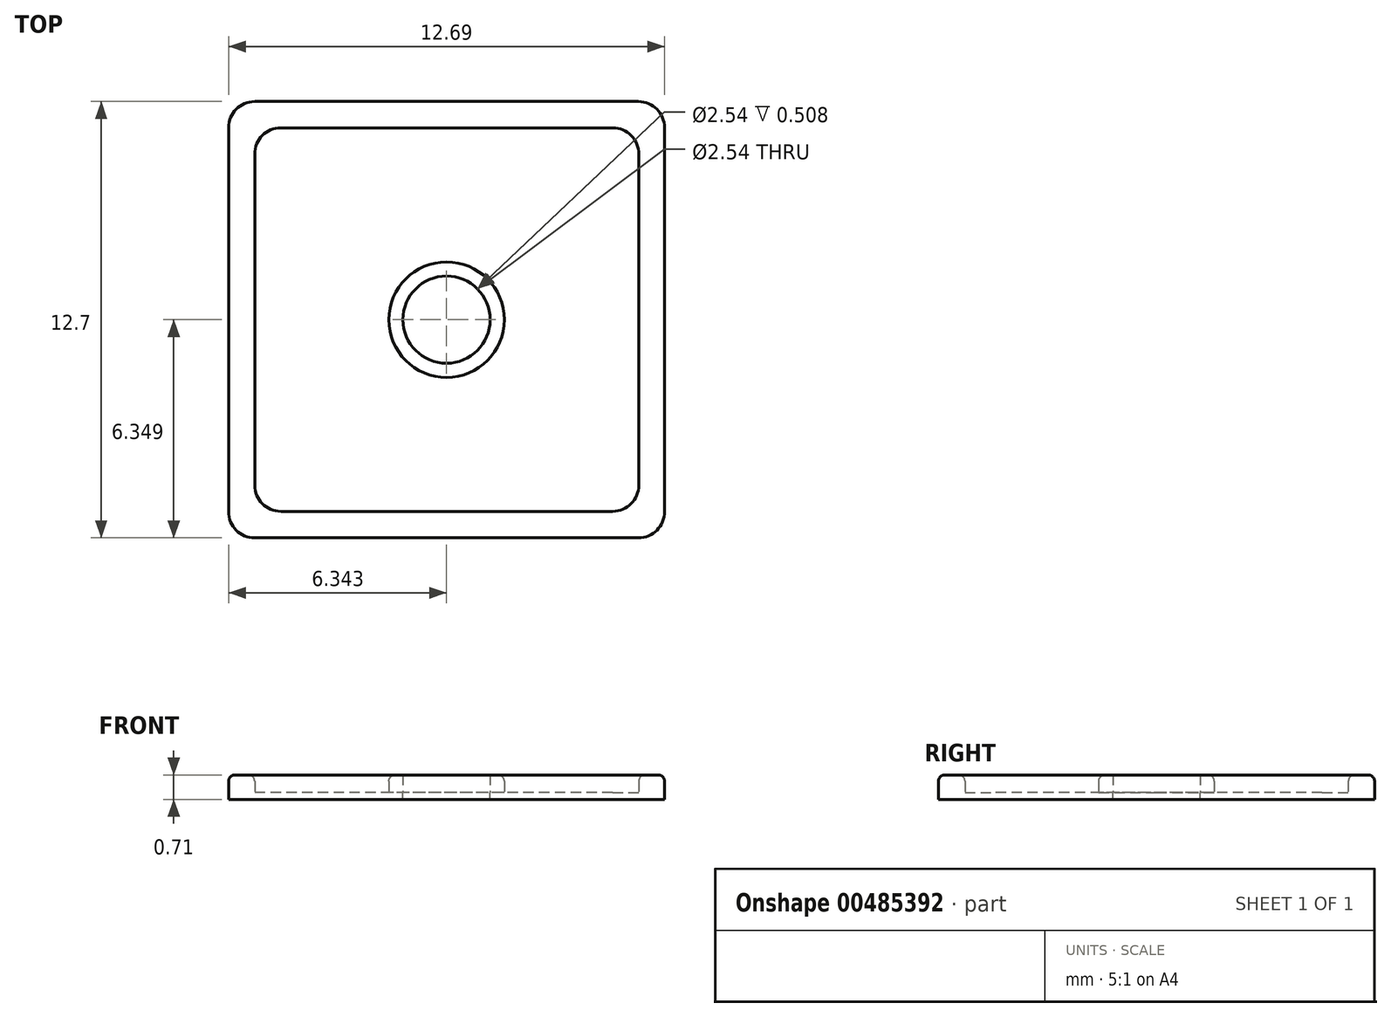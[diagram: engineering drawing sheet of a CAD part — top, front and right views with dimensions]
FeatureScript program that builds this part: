
annotation { "Feature Type Name" : "Feature", "Feature Type Description" : "" }
export const myFeature = defineFeature(function(context is Context, id is Id, definition is map)
    precondition{}
    {
        {
            var Q0;
            Q0=qCreatedBy(makeId("Top.planeOp"),FACE);
            var sketch = newSketch(context, id + "F0", { "sketchPlane" : qUnion([Q0])});
            skLineSegment(sketch, "E0.bottom", {"start": v(0, 0) * mm, "end": v(-12.7, 0) * mm});
            skLineSegment(sketch, "E0.top", {"start": v(0, 12.7) * mm, "end": v(-12.7, 12.7) * mm});
            skLineSegment(sketch, "E0.left", {"start": v(0, 0) * mm, "end": v(0, 12.7) * mm});
            skLineSegment(sketch, "E0.right", {"start": v(-12.7, 0) * mm, "end": v(-12.7, 12.7) * mm});
            skLineSegment(sketch, "E1", {"start": v(-6.35, 12.7) * mm, "end": v(-6.35, 11.93) * mm});
            skPoint(sketch, "E1.endSnap0", {"position": v(-6.35, 12.7) * mm});
            skLineSegment(sketch, "E2", {"start": v(-12.7, 6.35) * mm, "end": v(-11.93, 6.35) * mm});
            skLineSegment(sketch, "E3", {"start": v(-6.35, 11.93) * mm, "end": v(-11.93, 11.93) * mm});
            skLineSegment(sketch, "E4", {"start": v(-11.93, 11.93) * mm, "end": v(-11.93, 6.35) * mm});
            skLineSegment(sketch, "E5", {"start": v(-6.35, 0) * mm, "end": v(-6.35, 0.77) * mm});
            skLineSegment(sketch, "E6", {"start": v(0, 6.35) * mm, "end": v(-0.75, 6.35) * mm});
            skLineSegment(sketch, "E7", {"start": v(-0.75, 6.35) * mm, "end": v(-0.75, 0.77) * mm});
            skLineSegment(sketch, "E8", {"start": v(-0.75, 0.77) * mm, "end": v(-6.35, 0.77) * mm});
            skLineSegment(sketch, "E9", {"start": v(-6.35, 0.77) * mm, "end": v(-11.93, 0.77) * mm});
            skLineSegment(sketch, "E10", {"start": v(-11.93, 0.77) * mm, "end": v(-11.93, 6.35) * mm});
            skLineSegment(sketch, "E11", {"start": v(-6.35, 11.93) * mm, "end": v(-0.75, 11.93) * mm});
            skLineSegment(sketch, "E12", {"start": v(-0.75, 11.93) * mm, "end": v(-0.75, 6.35) * mm});
            skPoint(sketch, "E13", {"position": v(-6.35, 6.35) * mm});
            skSolve(sketch);
        }
        {
            var Q0;
            {var subQ4=sQuery(id+"F0.wireOp",EDGE,"E1");Q0=makeQuery(id+"F0.imprint","IMPRINT",FACE,{"disambiguationData":[TD([[makeQuery(id+"F0.imprint","IMPRINT",EDGE,{"derivedFrom":subQ4}),-1.0]])]});}
            var Q1;
            {var subQ4=sQuery(id+"F0.wireOp",EDGE,"E1");Q1=makeQuery(id+"F0.imprint","IMPRINT",FACE,{"disambiguationData":[TD([[makeQuery(id+"F0.imprint","IMPRINT",EDGE,{"derivedFrom":subQ4}),1.0]])]});}
            var Q2;
            {var subQ1=sQuery(id+"F0.wireOp",EDGE,"E5");Q2=makeQuery(id+"F0.imprint","IMPRINT",FACE,{"disambiguationData":[TD([[makeQuery(id+"F0.imprint","IMPRINT",EDGE,{"derivedFrom":subQ1}),-1.0]])]});}
            var Q3;
            {var subQ4=sQuery(id+"F0.wireOp",EDGE,"E2");Q3=makeQuery(id+"F0.imprint","IMPRINT",FACE,{"disambiguationData":[TD([[makeQuery(id+"F0.imprint","IMPRINT",EDGE,{"derivedFrom":subQ4}),-1.0]])]});}
            extrude(context, id + "F1", {"entities" : qUnion([Q0, Q1, Q2, Q3]), "depth" : 0.5 * mm});
        }
        {
            var Q0;
            Q0=makeQuery(id+"F0.imprint","IMPRINT",FACE,{"disambiguationData":[TD([[makeQuery(id+"F0.imprint","IMPRINT",EDGE,{"derivedFrom":sQuery(id+"F0.wireOp",EDGE,"E3")}),1.0]])]});
            var Q1;
            {var subQ4=sQuery(id+"F0.wireOp",EDGE,"E1");Q1=makeQuery(id+"F0.imprint","IMPRINT",FACE,{"disambiguationData":[TD([[makeQuery(id+"F0.imprint","IMPRINT",EDGE,{"derivedFrom":subQ4}),-1.0]])]});}
            var Q2;
            {var subQ4=sQuery(id+"F0.wireOp",EDGE,"E2");Q2=makeQuery(id+"F0.imprint","IMPRINT",FACE,{"disambiguationData":[TD([[makeQuery(id+"F0.imprint","IMPRINT",EDGE,{"derivedFrom":subQ4}),-1.0]])]});}
            var Q3;
            {var subQ1=sQuery(id+"F0.wireOp",EDGE,"E5");Q3=makeQuery(id+"F0.imprint","IMPRINT",FACE,{"disambiguationData":[TD([[makeQuery(id+"F0.imprint","IMPRINT",EDGE,{"derivedFrom":subQ1}),-1.0]])]});}
            var Q4;
            {var subQ4=sQuery(id+"F0.wireOp",EDGE,"E1");Q4=makeQuery(id+"F0.imprint","IMPRINT",FACE,{"disambiguationData":[TD([[makeQuery(id+"F0.imprint","IMPRINT",EDGE,{"derivedFrom":subQ4}),1.0]])]});}
            extrude(context, id + "F2", {"entities" : qUnion([Q0, Q1, Q2, Q3, Q4]), "operationType" : NewBodyOperationType.ADD, "oppositeDirection" : true, "depth" : 0.2 * mm});
        }
        {
            var Q0;
            {var subQ0=sQuery(id+"F0.wireOp",EDGE,"E0.left");var subQ1=sQuery(id+"F0.wireOp",EDGE,"E0.bottom");Q0=makeQuery(id+"F2.boolean.opBoolean","MERGE",EDGE,{"derivedFrom":[makeQuery(id+"F1.opExtrude","SWEPT_EDGE",EDGE,{"disambiguationData":[OSD([subQ1,subQ0])]}),makeQuery(id+"F2.opExtrude","SWEPT_EDGE",EDGE,{"disambiguationData":[OSD([subQ1,subQ0])]})]});}
            var Q1;
            {var subQ0=sQuery(id+"F0.wireOp",EDGE,"E0.left");var subQ1=sQuery(id+"F0.wireOp",EDGE,"E0.top");Q1=makeQuery(id+"F2.boolean.opBoolean","MERGE",EDGE,{"derivedFrom":[makeQuery(id+"F1.opExtrude","SWEPT_EDGE",EDGE,{"disambiguationData":[OSD([subQ1,subQ0])]}),makeQuery(id+"F2.opExtrude","SWEPT_EDGE",EDGE,{"disambiguationData":[OSD([subQ1,subQ0])]})]});}
            var Q2;
            {var subQ0=sQuery(id+"F0.wireOp",EDGE,"E0.right");var subQ1=sQuery(id+"F0.wireOp",EDGE,"E0.top");Q2=makeQuery(id+"F2.boolean.opBoolean","MERGE",EDGE,{"derivedFrom":[makeQuery(id+"F1.opExtrude","SWEPT_EDGE",EDGE,{"disambiguationData":[OSD([subQ1,subQ0])]}),makeQuery(id+"F2.opExtrude","SWEPT_EDGE",EDGE,{"disambiguationData":[OSD([subQ1,subQ0])]})]});}
            var Q3;
            {var subQ0=sQuery(id+"F0.wireOp",EDGE,"E0.right");var subQ1=sQuery(id+"F0.wireOp",EDGE,"E0.bottom");Q3=makeQuery(id+"F2.boolean.opBoolean","MERGE",EDGE,{"derivedFrom":[makeQuery(id+"F1.opExtrude","SWEPT_EDGE",EDGE,{"disambiguationData":[OSD([subQ1,subQ0])]}),makeQuery(id+"F2.opExtrude","SWEPT_EDGE",EDGE,{"disambiguationData":[OSD([subQ1,subQ0])]})]});}
            var Q4;
            Q4=makeQuery(id+"F1.opExtrude","SWEPT_EDGE",EDGE,{"disambiguationData":[OSD([sQuery(id+"F0.wireOp",EDGE,"E3"),sQuery(id+"F0.wireOp",EDGE,"E4")])]});
            var Q5;
            Q5=makeQuery(id+"F1.opExtrude","SWEPT_EDGE",EDGE,{"disambiguationData":[OSD([sQuery(id+"F0.wireOp",EDGE,"E9"),sQuery(id+"F0.wireOp",EDGE,"E10")])]});
            var Q6;
            Q6=makeQuery(id+"F1.opExtrude","SWEPT_EDGE",EDGE,{"disambiguationData":[OSD([sQuery(id+"F0.wireOp",EDGE,"E11"),sQuery(id+"F0.wireOp",EDGE,"E12")])]});
            var Q7;
            Q7=makeQuery(id+"F1.opExtrude","SWEPT_EDGE",EDGE,{"disambiguationData":[OSD([sQuery(id+"F0.wireOp",EDGE,"E7"),sQuery(id+"F0.wireOp",EDGE,"E8")])]});
            fillet(context, id + "F3", {"entities" : qUnion([Q0, Q1, Q2, Q3, Q4, Q5, Q6, Q7]), "radius" : 0.76 * mm, "tangentPropagation" : true, "allowEdgeOverflow" : false});
        }
        {
            var Q0;
            Q0=makeQuery(id+"F0.imprint","IMPRINT",FACE,{"disambiguationData":[TD([[makeQuery(id+"F0.imprint","IMPRINT",EDGE,{"derivedFrom":sQuery(id+"F0.wireOp",EDGE,"E3")}),1.0]])]});
            cPlane(context, id + "F4", {"entities" : qUnion([Q0]), "cplaneType" : CPlaneType.OFFSET, "offset" : 0 * mm, "width" : 152.4 * mm, "height" : 152.4 * mm});
        }
        {
            var Q0;
            Q0=qCreatedBy(id+"F4.planeOp",FACE);
            var sketch = newSketch(context, id + "F5", { "sketchPlane" : qUnion([Q0])});
            skCircle(sketch, "E14", {"center": v(-6.35, 6.35) * mm, "radius": 1.68 * mm});
            skSolve(sketch);
        }
        {
            var Q0;
            Q0 = qSketchRegion(id + "F5", true);
            extrude(context, id + "F6", {"entities" : qUnion([Q0]), "operationType" : NewBodyOperationType.ADD, "depth" : 0.5 * mm});
        }
        {
            var Q0;
            Q0=sQuery(id+"F5.wireOp",VERTEX,"E14.center");
            var Q1;
            Q1=makeQuery(id+"F1.opExtrude","SWEPT_BODY",BODY,{"disambiguationData":[OSD([sQuery(id+"F0.wireOp",EDGE,"E0.bottom"),sQuery(id+"F0.wireOp",EDGE,"E0.top"),sQuery(id+"F0.wireOp",EDGE,"E0.left"),sQuery(id+"F0.wireOp",EDGE,"E0.right"),sQuery(id+"F0.wireOp",EDGE,"E3"),sQuery(id+"F0.wireOp",EDGE,"E4"),sQuery(id+"F0.wireOp",EDGE,"E7"),sQuery(id+"F0.wireOp",EDGE,"E8"),sQuery(id+"F0.wireOp",EDGE,"E9"),sQuery(id+"F0.wireOp",EDGE,"E10"),sQuery(id+"F0.wireOp",EDGE,"E11"),sQuery(id+"F0.wireOp",EDGE,"E12")])]});
            hole(context, id + "F7", {"style" : HoleStyle.SIMPLE, "endStyle" : HoleEndStyle.THROUGH, "oppositeDirection" : true, "holeDiameter" : 2.54 * mm, "isTappedThrough" : true, "tappedDepth" : 12.7 * mm, "tapClearance" : 3, "locations" : qUnion([Q0]), "scope" : qUnion([Q1])});
        }
        {
            var Q0;
            Q0=sQuery(id+"F0.wireOp",VERTEX,"E13");
            var Q1;
            Q1=makeQuery(id+"F1.opExtrude","SWEPT_BODY",BODY,{"disambiguationData":[OSD([sQuery(id+"F0.wireOp",EDGE,"E0.bottom"),sQuery(id+"F0.wireOp",EDGE,"E0.top"),sQuery(id+"F0.wireOp",EDGE,"E0.left"),sQuery(id+"F0.wireOp",EDGE,"E0.right"),sQuery(id+"F0.wireOp",EDGE,"E3"),sQuery(id+"F0.wireOp",EDGE,"E4"),sQuery(id+"F0.wireOp",EDGE,"E7"),sQuery(id+"F0.wireOp",EDGE,"E8"),sQuery(id+"F0.wireOp",EDGE,"E9"),sQuery(id+"F0.wireOp",EDGE,"E10"),sQuery(id+"F0.wireOp",EDGE,"E11"),sQuery(id+"F0.wireOp",EDGE,"E12")])]});
            hole(context, id + "F8", {"style" : HoleStyle.SIMPLE, "endStyle" : HoleEndStyle.THROUGH, "holeDiameter" : 2.54 * mm, "isTappedThrough" : true, "tappedDepth" : 12.7 * mm, "tapClearance" : 3, "locations" : qUnion([Q0]), "scope" : qUnion([Q1])});
        }
        {
            var Q0;
            Q0=makeQuery(id+"F7.hole-0.boolean.opBoolean","INTERSECT",EDGE,{"derivedFrom":[makeQuery(id+"F6.opExtrude","CAP_FACE",FACE,{"disambiguationData":[OSD([sQuery(id+"F5.wireOp",EDGE,"E14")])],"isStart":false}),makeQuery(id+"F7.hole-0.opRevolve","SWEPT_FACE",FACE,{"disambiguationData":[OSD([sQuery(id+"F7.hole-0.sketch.wireOp",EDGE,"core_line_2")])]})]});
            var Q1;
            Q1=makeQuery(id+"F6.opExtrude","CAP_EDGE",EDGE,{"disambiguationData":[OSD([sQuery(id+"F5.wireOp",EDGE,"E14")])],"isStart":false});
            var Q2;
            Q2=makeQuery(id+"F1.opExtrude","CAP_EDGE",EDGE,{"disambiguationData":[OSD([sQuery(id+"F0.wireOp",EDGE,"E0.left")])],"isStart":false});
            var Q3;
            Q3=makeQuery(id+"F1.opExtrude","CAP_EDGE",EDGE,{"disambiguationData":[OSD([sQuery(id+"F0.wireOp",EDGE,"E7"),sQuery(id+"F0.wireOp",EDGE,"E12")])],"isStart":false});
            fillet(context, id + "F9", {"entities" : qUnion([Q0, Q1, Q2, Q3]), "radius" : 0.18 * mm, "tangentPropagation" : true, "allowEdgeOverflow" : false});
        }
    });
